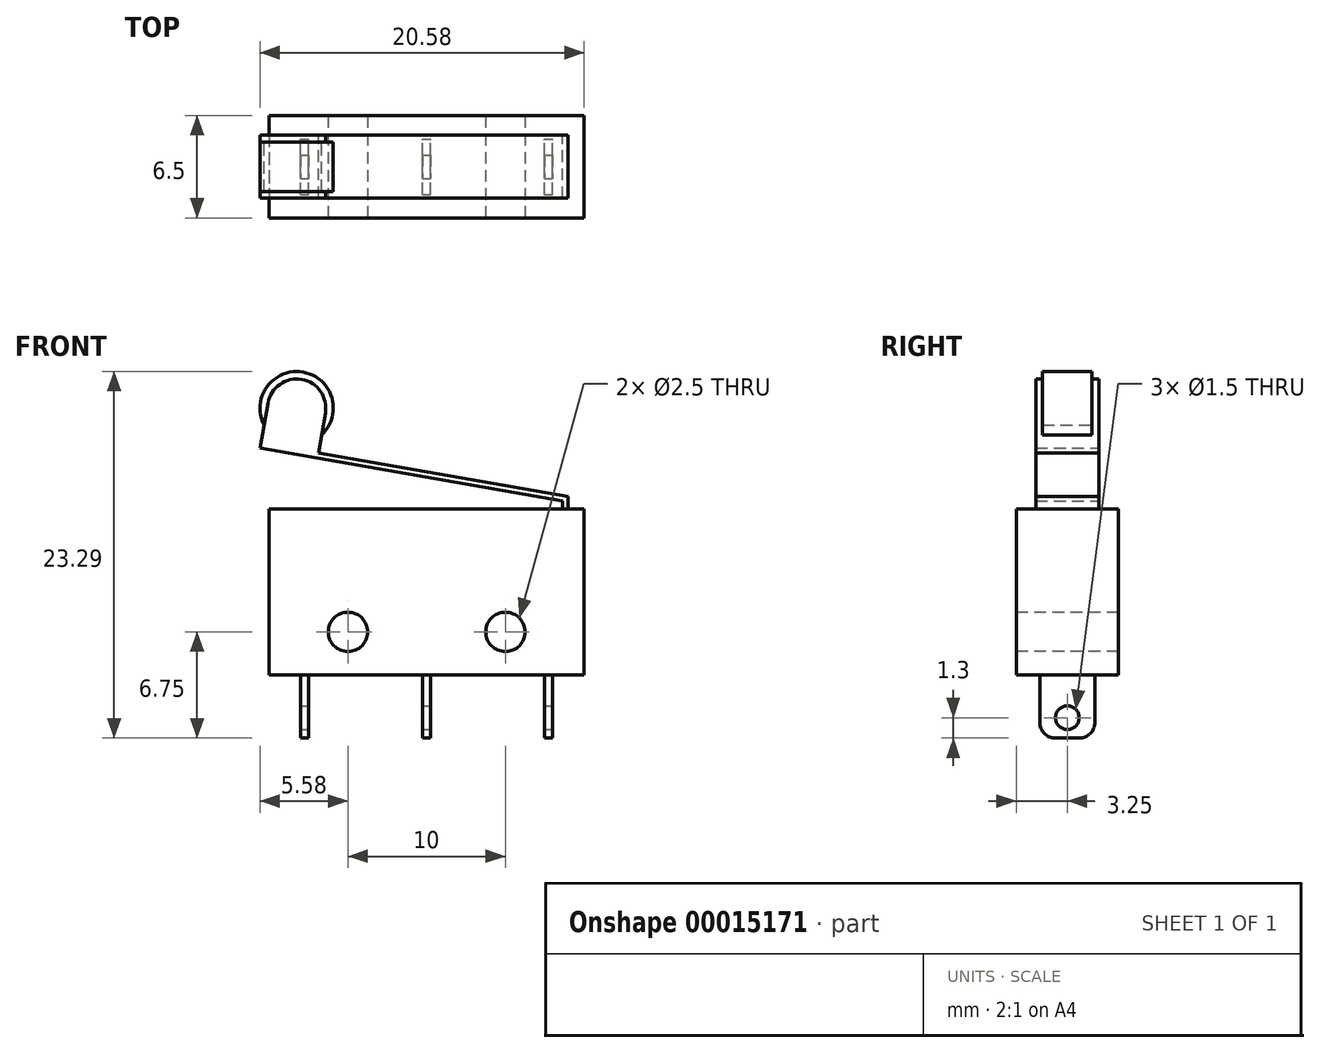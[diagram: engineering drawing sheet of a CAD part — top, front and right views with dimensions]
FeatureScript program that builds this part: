
annotation { "Feature Type Name" : "Feature", "Feature Type Description" : "" }
export const myFeature = defineFeature(function(context is Context, id is Id, definition is map)
    precondition{}
    {
        {
            var Q0;
            Q0=qCreatedBy(makeId("Top.planeOp"),FACE);
            var sketch = newSketch(context, id + "F0", { "sketchPlane" : qUnion([Q0])});
            skLineSegment(sketch, "E0.bottom", {"start": v(-10, 3.25) * mm, "end": v(10, 3.25) * mm});
            skLineSegment(sketch, "E0.top", {"start": v(-10, -3.25) * mm, "end": v(10, -3.25) * mm});
            skLineSegment(sketch, "E0.left", {"start": v(-10, 3.25) * mm, "end": v(-10, -3.25) * mm});
            skLineSegment(sketch, "E0.right", {"start": v(10, 3.25) * mm, "end": v(10, -3.25) * mm});
            skPoint(sketch, "E1", {"position": v(-10, 0) * mm});
            skPoint(sketch, "E2", {"position": v(0, 3.25) * mm});
            skLineSegment(sketch, "E3.bottom", {"start": v(-8, -1.75) * mm, "end": v(-7.5, -1.75) * mm});
            skLineSegment(sketch, "E3.top", {"start": v(-8, 1.75) * mm, "end": v(-7.5, 1.75) * mm});
            skLineSegment(sketch, "E3.left", {"start": v(-8, -1.75) * mm, "end": v(-8, 1.75) * mm});
            skLineSegment(sketch, "E3.right", {"start": v(-7.5, -1.75) * mm, "end": v(-7.5, 1.75) * mm});
            skLineSegment(sketch, "E4.bottom", {"start": v(-0.25, -1.75) * mm, "end": v(0.25, -1.75) * mm});
            skLineSegment(sketch, "E4.top", {"start": v(-0.25, 1.75) * mm, "end": v(0.25, 1.75) * mm});
            skLineSegment(sketch, "E4.left", {"start": v(-0.25, -1.75) * mm, "end": v(-0.25, 1.75) * mm});
            skLineSegment(sketch, "E4.right", {"start": v(0.25, -1.75) * mm, "end": v(0.25, 1.75) * mm});
            skLineSegment(sketch, "E5.bottom", {"start": v(7.5, -1.75) * mm, "end": v(8, -1.75) * mm});
            skLineSegment(sketch, "E5.top", {"start": v(7.5, 1.75) * mm, "end": v(8, 1.75) * mm});
            skLineSegment(sketch, "E5.left", {"start": v(7.5, -1.75) * mm, "end": v(7.5, 1.75) * mm});
            skLineSegment(sketch, "E5.right", {"start": v(8, -1.75) * mm, "end": v(8, 1.75) * mm});
            skPoint(sketch, "E6", {"position": v(-7.75, -1.75) * mm});
            skPoint(sketch, "E7", {"position": v(-8, 0) * mm});
            skPoint(sketch, "E8", {"position": v(-0.25, 0) * mm});
            skPoint(sketch, "E9", {"position": v(0, -1.75) * mm});
            skPoint(sketch, "E10", {"position": v(7.5, 0) * mm});
            skLineSegment(sketch, "E11", {"start": v(-8, 0) * mm, "end": v(-10, 0) * mm, "construction": true});
            skLineSegment(sketch, "E12", {"start": v(8, 0) * mm, "end": v(10, 0) * mm, "construction": true});
            skPoint(sketch, "E13", {"position": v(0.25, 0) * mm});
            skSolve(sketch);
        }
        {
            var Q0;
            Q0 = qSketchRegion(id + "F0", true);
            var Q1;
            Q1=makeQuery(id+"F0.imprint","IMPRINT",FACE,{"disambiguationData":[TD([[makeQuery(id+"F0.imprint","IMPRINT",EDGE,{"derivedFrom":sQuery(id+"F0.wireOp",EDGE,"E3.bottom")}),1.0]])]});
            var Q2;
            Q2=makeQuery(id+"F0.imprint","IMPRINT",FACE,{"disambiguationData":[TD([[makeQuery(id+"F0.imprint","IMPRINT",EDGE,{"derivedFrom":sQuery(id+"F0.wireOp",EDGE,"E4.bottom")}),1.0]])]});
            var Q3;
            Q3=makeQuery(id+"F0.imprint","IMPRINT",FACE,{"disambiguationData":[TD([[makeQuery(id+"F0.imprint","IMPRINT",EDGE,{"derivedFrom":sQuery(id+"F0.wireOp",EDGE,"E5.bottom")}),1.0]])]});
            extrude(context, id + "F1", {"entities" : qUnion([Q0, Q1, Q2, Q3]), "depth" : 10.57 * mm});
        }
        {
            var Q0;
            Q0=makeQuery(id+"F0.imprint","IMPRINT",FACE,{"disambiguationData":[TD([[makeQuery(id+"F0.imprint","IMPRINT",EDGE,{"derivedFrom":sQuery(id+"F0.wireOp",EDGE,"E3.bottom")}),1.0]])]});
            var Q1;
            Q1=makeQuery(id+"F0.imprint","IMPRINT",FACE,{"disambiguationData":[TD([[makeQuery(id+"F0.imprint","IMPRINT",EDGE,{"derivedFrom":sQuery(id+"F0.wireOp",EDGE,"E4.bottom")}),1.0]])]});
            var Q2;
            Q2=makeQuery(id+"F0.imprint","IMPRINT",FACE,{"disambiguationData":[TD([[makeQuery(id+"F0.imprint","IMPRINT",EDGE,{"derivedFrom":sQuery(id+"F0.wireOp",EDGE,"E5.bottom")}),1.0]])]});
            extrude(context, id + "F2", {"entities" : qUnion([Q0, Q1, Q2]), "operationType" : NewBodyOperationType.ADD, "oppositeDirection" : true, "depth" : 4 * mm});
        }
        {
            var Q0;
            Q0=makeQuery(id+"F2.opExtrude","CAP_EDGE",EDGE,{"disambiguationData":[OSD([sQuery(id+"F0.wireOp",EDGE,"E5.top")])],"isStart":false});
            var Q1;
            Q1=makeQuery(id+"F2.opExtrude","CAP_EDGE",EDGE,{"disambiguationData":[OSD([sQuery(id+"F0.wireOp",EDGE,"E4.top")])],"isStart":false});
            var Q2;
            Q2=makeQuery(id+"F2.opExtrude","CAP_EDGE",EDGE,{"disambiguationData":[OSD([sQuery(id+"F0.wireOp",EDGE,"E3.top")])],"isStart":false});
            var Q3;
            Q3=makeQuery(id+"F2.opExtrude","CAP_EDGE",EDGE,{"disambiguationData":[OSD([sQuery(id+"F0.wireOp",EDGE,"E5.bottom")])],"isStart":false});
            var Q4;
            Q4=makeQuery(id+"F2.opExtrude","CAP_EDGE",EDGE,{"disambiguationData":[OSD([sQuery(id+"F0.wireOp",EDGE,"E4.bottom")])],"isStart":false});
            var Q5;
            Q5=makeQuery(id+"F2.opExtrude","CAP_EDGE",EDGE,{"disambiguationData":[OSD([sQuery(id+"F0.wireOp",EDGE,"E3.bottom")])],"isStart":false});
            fillet(context, id + "F3", {"entities" : qUnion([Q0, Q1, Q2, Q3, Q4, Q5]), "radius" : 1 * mm, "tangentPropagation" : true, "allowEdgeOverflow" : false});
        }
        {
            var Q0;
            Q0=makeQuery(id+"F2.opExtrude","SWEPT_FACE",FACE,{"disambiguationData":[OSD([sQuery(id+"F0.wireOp",EDGE,"E5.right")])]});
            var sketch = newSketch(context, id + "F4", { "sketchPlane" : qUnion([Q0])});
            skCircle(sketch, "E14", {"center": v(0, -2.7) * mm, "radius": 0.75 * mm});
            skSolve(sketch);
        }
        {
            var Q0;
            Q0=makeQuery(id+"F4.imprint","IMPRINT",FACE,{"disambiguationData":[TD([[makeQuery(id+"F4.imprint","IMPRINT",EDGE,{"derivedFrom":sQuery(id+"F4.wireOp",EDGE,"E14")}),1.0]])]});
            extrude(context, id + "F5", {"entities" : qUnion([Q0]), "operationType" : NewBodyOperationType.REMOVE, "oppositeDirection" : true, "depth" : 25 * mm});
        }
        {
            var Q0;
            Q0=qCreatedBy(makeId("Front.planeOp"),FACE);
            var sketch = newSketch(context, id + "F6", { "sketchPlane" : qUnion([Q0])});
            skLineSegment(sketch, "E15", {"start": v(8.63, 10.57) * mm, "end": v(8.63, 11.07) * mm});
            skLineSegment(sketch, "E16", {"start": v(8.63, 11.07) * mm, "end": v(-10.58, 14.42) * mm});
            skLineSegment(sketch, "E17", {"start": v(-10.58, 14.42) * mm, "end": v(-10.08, 17.28) * mm});
            skLineSegment(sketch, "E18", {"start": v(-6.44, 16.65) * mm, "end": v(-6.87, 14.13) * mm});
            skLineSegment(sketch, "E19.0", {"start": v(8.98, 11.36) * mm, "end": v(-6.87, 14.13) * mm});
            skLineSegment(sketch, "E19.1", {"start": v(8.98, 10.57) * mm, "end": v(8.98, 11.36) * mm});
            skCircle(sketch, "E20", {"center": v(-8.26, 16.96) * mm, "radius": 2.33 * mm});
            skArc(sketch, "E21", {"start": v(-6.44, 16.65) * mm, "mid": v(-7.94, 18.79) * mm, "end": v(-10.08, 17.28) * mm});
            skLineSegment(sketch, "E22", {"start": v(8.98, 10.57) * mm, "end": v(8.63, 10.57) * mm});
            skCircle(sketch, "E23", {"center": v(5, 2.75) * mm, "radius": 1.25 * mm});
            skCircle(sketch, "E24", {"center": v(-5, 2.75) * mm, "radius": 1.25 * mm});
            skLineSegment(sketch, "E25.0.0", {"start": v(10, 0) * mm, "end": v(-10, 0) * mm});
            skLineSegment(sketch, "E25.0.1", {"start": v(-10, 0) * mm, "end": v(-10, 10.57) * mm});
            skLineSegment(sketch, "E25.0.2", {"start": v(-10, 10.57) * mm, "end": v(10, 10.57) * mm});
            skLineSegment(sketch, "E25.0.3", {"start": v(10, 10.57) * mm, "end": v(10, 0) * mm});
            skLineSegment(sketch, "E26", {"start": v(5, 2.75) * mm, "end": v(10, 2.75) * mm, "construction": true});
            skLineSegment(sketch, "E27", {"start": v(5, 2.75) * mm, "end": v(5, 0) * mm, "construction": true});
            skLineSegment(sketch, "E28", {"start": v(-5, 2.75) * mm, "end": v(-10, 2.75) * mm, "construction": true});
            skSolve(sketch);
        }
        {
            var Q0;
            Q0=makeQuery(id+"F6.imprint","IMPRINT",FACE,{"disambiguationData":[TD([[makeQuery(id+"F6.imprint","IMPRINT",EDGE,{"derivedFrom":sQuery(id+"F6.wireOp",EDGE,"E15")}),-1.0]])]});
            var Q1;
            {var subQ0=sQuery(id+"F6.wireOp",EDGE,"E21");Q1=makeQuery(id+"F6.imprint","IMPRINT",FACE,{"disambiguationData":[TD([[makeQuery(id+"F6.imprint","IMPRINT",EDGE,{"derivedFrom":subQ0}),1.0]])]});}
            var Q2;
            {var subQ1=sQuery(id+"F6.wireOp",EDGE,"E16");Q2=makeQuery(id+"F6.imprint","IMPRINT",FACE,{"disambiguationData":[TD([[makeQuery(id+"F6.imprint","IMPRINT",EDGE,{"derivedFrom":subQ1}),-1.0]])]});}
            extrude(context, id + "F7", {"entities" : qUnion([Q0, Q1, Q2]), "operationType" : NewBodyOperationType.ADD, "depth" : 4 * mm, "symmetric" : true});
        }
        {
            var Q0;
            {var subQ0=sQuery(id+"F6.wireOp",EDGE,"E21");Q0=makeQuery(id+"F6.imprint","IMPRINT",FACE,{"disambiguationData":[TD([[makeQuery(id+"F6.imprint","IMPRINT",EDGE,{"derivedFrom":subQ0}),-1.0]])]});}
            var Q1;
            {var subQ0=sQuery(id+"F6.wireOp",EDGE,"E21");Q1=makeQuery(id+"F6.imprint","IMPRINT",FACE,{"disambiguationData":[TD([[makeQuery(id+"F6.imprint","IMPRINT",EDGE,{"derivedFrom":subQ0}),1.0]])]});}
            extrude(context, id + "F8", {"entities" : qUnion([Q0, Q1]), "operationType" : NewBodyOperationType.ADD, "depth" : 3.15 * mm, "symmetric" : true});
        }
        {
            var Q0;
            Q0=makeQuery(id+"F6.imprint","IMPRINT",FACE,{"disambiguationData":[TD([[makeQuery(id+"F6.imprint","IMPRINT",EDGE,{"derivedFrom":sQuery(id+"F6.wireOp",EDGE,"E23")}),1.0]])]});
            var Q1;
            Q1=makeQuery(id+"F6.imprint","IMPRINT",FACE,{"disambiguationData":[TD([[makeQuery(id+"F6.imprint","IMPRINT",EDGE,{"derivedFrom":sQuery(id+"F6.wireOp",EDGE,"E24")}),1.0]])]});
            extrude(context, id + "F9", {"entities" : qUnion([Q0, Q1]), "operationType" : NewBodyOperationType.REMOVE, "oppositeDirection" : true, "depth" : 25 * mm, "symmetric" : true});
        }
    });
